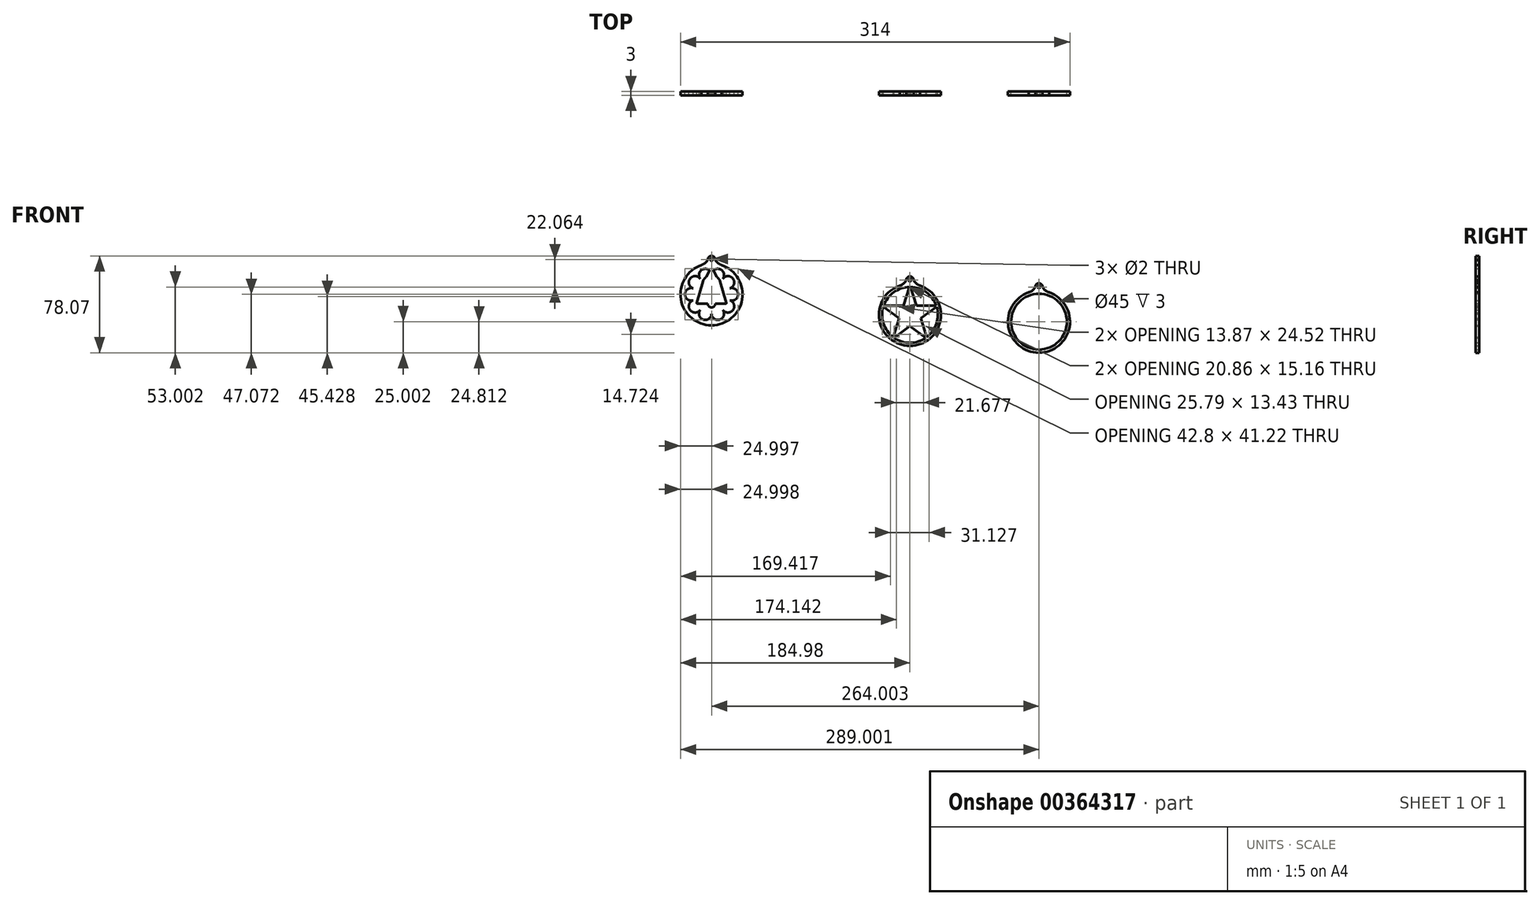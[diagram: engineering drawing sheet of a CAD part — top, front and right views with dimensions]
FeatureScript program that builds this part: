
annotation { "Feature Type Name" : "Feature", "Feature Type Description" : "" }
export const myFeature = defineFeature(function(context is Context, id is Id, definition is map)
    precondition{}
    {
        {
            var Q0;
            Q0=qCreatedBy(makeId("Front.planeOp"),FACE);
            var sketch = newSketch(context, id + "F0", { "sketchPlane" : qUnion([Q0])});
            skArc(sketch, "E0", {"start": v(-7.91, 23.72) * mm, "mid": v(0.08, -25) * mm, "end": v(7.76, 23.77) * mm});
            skPoint(sketch, "E1", {"position": v(0, 28) * mm});
            skArc(sketch, "E2", {"start": v(3, 27.85) * mm, "mid": v(0.08, 31) * mm, "end": v(-3, 28) * mm});
            skArc(sketch, "E3", {"start": v(3, 27.85) * mm, "mid": v(5.2, 25.22) * mm, "end": v(8.22, 23.6) * mm});
            skArc(sketch, "E4", {"start": v(-8.22, 23.6) * mm, "mid": v(-5.18, 25.29) * mm, "end": v(-3, 28) * mm});
            skCircle(sketch, "E5", {"center": v(0, 28) * mm, "radius": 1 * mm});
            skArc(sketch, "E6", {"start": v(-0.4, 22.5) * mm, "mid": v(-13.23, 18.2) * mm, "end": v(-21.27, 7.34) * mm});
            skCircle(sketch, "E7.cCircle", {"center": v(0, 0) * mm, "radius": 23.75 * mm, "construction": true});
            skLineSegment(sketch, "E8", {"start": v(-21.27, 7.34) * mm, "end": v(-5.33, 7.34) * mm});
            skLineSegment(sketch, "E9", {"start": v(21.52, 6.56) * mm, "end": v(8.63, -2.8) * mm});
            skLineSegment(sketch, "E10", {"start": v(-13.55, -17.96) * mm, "end": v(-8.63, -2.8) * mm});
            skLineSegment(sketch, "E11", {"start": v(0.4, 22.5) * mm, "end": v(5.33, 7.34) * mm});
            skLineSegment(sketch, "E12", {"start": v(-21.52, 6.56) * mm, "end": v(-8.63, -2.8) * mm});
            skArc(sketch, "E13.trimOffspring", {"start": v(21.27, 7.34) * mm, "mid": v(13.23, 18.2) * mm, "end": v(0.4, 22.5) * mm});
            skLineSegment(sketch, "E14.trimOffspring", {"start": v(8.63, -2.8) * mm, "end": v(13.55, -17.96) * mm});
            skLineSegment(sketch, "E15.trimOffspring", {"start": v(5.33, 7.34) * mm, "end": v(21.27, 7.34) * mm});
            skLineSegment(sketch, "E16.trimOffspring", {"start": v(-5.33, 7.34) * mm, "end": v(-0.4, 22.5) * mm});
            skLineSegment(sketch, "E17.trimOffspring", {"start": v(0, -9.07) * mm, "end": v(12.9, -18.44) * mm});
            skLineSegment(sketch, "E18.trimOffspring", {"start": v(0, -9.07) * mm, "end": v(-12.9, -18.44) * mm});
            skArc(sketch, "E19.trimOffspring", {"start": v(-21.52, 6.56) * mm, "mid": v(-21.4, -6.95) * mm, "end": v(-13.55, -17.96) * mm});
            skArc(sketch, "E20.trimOffspring", {"start": v(13.55, -17.96) * mm, "mid": v(21.4, -6.95) * mm, "end": v(21.52, 6.56) * mm});
            skArc(sketch, "E21.trimOffspring", {"start": v(-12.9, -18.44) * mm, "mid": v(0, -22.5) * mm, "end": v(12.9, -18.44) * mm});
            skArc(sketch, "E22", {"start": v(96.11, 18.2) * mm, "mid": v(104.1, -30.5) * mm, "end": v(111.78, 18.26) * mm});
            skPoint(sketch, "E23", {"position": v(104.02, 22.5) * mm});
            skArc(sketch, "E24", {"start": v(107.02, 22.34) * mm, "mid": v(104.1, 25.5) * mm, "end": v(101.02, 22.5) * mm});
            skArc(sketch, "E25", {"start": v(107.02, 22.34) * mm, "mid": v(109.22, 19.71) * mm, "end": v(112.24, 18.1) * mm});
            skArc(sketch, "E26", {"start": v(95.8, 18.1) * mm, "mid": v(98.84, 19.78) * mm, "end": v(101.02, 22.5) * mm});
            skCircle(sketch, "E27", {"center": v(104.02, 22.5) * mm, "radius": 1 * mm});
            skCircle(sketch, "E28.cCircle", {"center": v(104.02, -5.5) * mm, "radius": 23.75 * mm, "construction": true});
            skCircle(sketch, "E29", {"center": v(104.02, -5.5) * mm, "radius": 22.5 * mm});
            skArc(sketch, "E30", {"start": v(-167.9, 40.27) * mm, "mid": v(-159.9, -8.44) * mm, "end": v(-152.22, 40.32) * mm});
            skPoint(sketch, "E31", {"position": v(-159.98, 44.56) * mm});
            skArc(sketch, "E32", {"start": v(-156.99, 44.4) * mm, "mid": v(-159.9, 47.56) * mm, "end": v(-162.98, 44.56) * mm});
            skArc(sketch, "E33", {"start": v(-156.99, 44.4) * mm, "mid": v(-154.78, 41.78) * mm, "end": v(-151.76, 40.16) * mm});
            skArc(sketch, "E34", {"start": v(-168.2, 40.16) * mm, "mid": v(-165.16, 41.85) * mm, "end": v(-162.98, 44.56) * mm});
            skCircle(sketch, "E35", {"center": v(-159.98, 44.56) * mm, "radius": 1 * mm});
            skCircle(sketch, "E36.cCircle", {"center": v(-159.98, 16.56) * mm, "radius": 23.75 * mm, "construction": true});
            skLineSegment(sketch, "E37.0", {"start": v(-153.44, 36.93) * mm, "end": v(-153.3, 36.89) * mm});
            skLineSegment(sketch, "E37.1", {"start": v(-142.71, 29.2) * mm, "end": v(-142.63, 29.08) * mm});
            skLineSegment(sketch, "E37.2", {"start": v(-138.58, 16.63) * mm, "end": v(-138.58, 16.49) * mm});
            skLineSegment(sketch, "E37.3", {"start": v(-142.63, 4.04) * mm, "end": v(-142.71, 3.92) * mm});
            skLineSegment(sketch, "E37.4", {"start": v(-153.3, -3.77) * mm, "end": v(-153.44, -3.82) * mm});
            skLineSegment(sketch, "E37.5", {"start": v(-166.53, -3.82) * mm, "end": v(-166.66, -3.77) * mm});
            skLineSegment(sketch, "E37.6", {"start": v(-177.25, 3.92) * mm, "end": v(-177.34, 4.04) * mm});
            skLineSegment(sketch, "E37.7", {"start": v(-181.38, 16.49) * mm, "end": v(-181.38, 16.63) * mm});
            skLineSegment(sketch, "E37.8", {"start": v(-177.34, 29.08) * mm, "end": v(-177.25, 29.2) * mm});
            skLineSegment(sketch, "E37.9", {"start": v(-166.66, 36.89) * mm, "end": v(-166.53, 36.93) * mm});
            skPoint(sketch, "E38.visualSharp", {"position": v(-173.2, 34.76) * mm});
            skArc(sketch, "E38.filletArc", {"start": v(-166.66, 36.89) * mm, "mid": v(-169.87, 33.68) * mm, "end": v(-169.16, 29.2) * mm});
            skPoint(sketch, "E39.visualSharp", {"position": v(-159.98, 39.06) * mm});
            skArc(sketch, "E39.filletArc", {"start": v(-162.02, 36.2) * mm, "mid": v(-164.18, 37.1) * mm, "end": v(-166.53, 36.93) * mm});
            skArc(sketch, "E40.filletArc", {"start": v(-153.44, 36.93) * mm, "mid": v(-155.78, 37.1) * mm, "end": v(-157.95, 36.2) * mm});
            skPoint(sketch, "E41.visualSharp", {"position": v(-146.76, 34.76) * mm});
            skArc(sketch, "E41.filletArc", {"start": v(-150.8, 29.2) * mm, "mid": v(-150.1, 33.68) * mm, "end": v(-153.3, 36.89) * mm});
            skArc(sketch, "E42.filletArc", {"start": v(-142.71, 29.2) * mm, "mid": v(-146.76, 31.25) * mm, "end": v(-150.8, 29.2) * mm});
            skPoint(sketch, "E43.visualSharp", {"position": v(-138.58, 23.5) * mm});
            skArc(sketch, "E43.filletArc", {"start": v(-145.13, 21.38) * mm, "mid": v(-141.92, 24.6) * mm, "end": v(-142.63, 29.08) * mm});
            skPoint(sketch, "E44.visualSharp", {"position": v(-138.58, 9.6) * mm});
            skArc(sketch, "E44.filletArc", {"start": v(-145.13, 11.73) * mm, "mid": v(-140.64, 12.44) * mm, "end": v(-138.58, 16.49) * mm});
            skArc(sketch, "E45.filletArc", {"start": v(-138.58, 16.63) * mm, "mid": v(-140.64, 20.67) * mm, "end": v(-145.13, 21.38) * mm});
            skPoint(sketch, "E46.visualSharp", {"position": v(-146.76, -1.65) * mm});
            skArc(sketch, "E46.filletArc", {"start": v(-150.8, 3.92) * mm, "mid": v(-146.76, 1.86) * mm, "end": v(-142.71, 3.92) * mm});
            skArc(sketch, "E47.filletArc", {"start": v(-142.63, 4.04) * mm, "mid": v(-141.92, 8.52) * mm, "end": v(-145.13, 11.73) * mm});
            skArc(sketch, "E48.filletArc", {"start": v(-153.3, -3.77) * mm, "mid": v(-150.1, -0.56) * mm, "end": v(-150.8, 3.92) * mm});
            skPoint(sketch, "E49.visualSharp", {"position": v(-159.98, -5.94) * mm});
            skArc(sketch, "E49.filletArc", {"start": v(-159.98, 0.94) * mm, "mid": v(-157.92, -3.1) * mm, "end": v(-153.44, -3.82) * mm});
            skArc(sketch, "E50.filletArc", {"start": v(-166.53, -3.82) * mm, "mid": v(-162.04, -3.1) * mm, "end": v(-159.98, 0.94) * mm});
            skPoint(sketch, "E51.visualSharp", {"position": v(-173.2, -1.65) * mm});
            skArc(sketch, "E51.filletArc", {"start": v(-169.16, 3.92) * mm, "mid": v(-169.87, -0.56) * mm, "end": v(-166.66, -3.77) * mm});
            skPoint(sketch, "E52.visualSharp", {"position": v(-181.38, 9.6) * mm});
            skArc(sketch, "E52.filletArc", {"start": v(-174.84, 11.73) * mm, "mid": v(-178.05, 8.52) * mm, "end": v(-177.34, 4.04) * mm});
            skArc(sketch, "E53.filletArc", {"start": v(-177.25, 3.92) * mm, "mid": v(-173.2, 1.86) * mm, "end": v(-169.16, 3.92) * mm});
            skPoint(sketch, "E54.visualSharp", {"position": v(-181.38, 23.5) * mm});
            skArc(sketch, "E54.filletArc", {"start": v(-174.84, 21.38) * mm, "mid": v(-179.32, 20.67) * mm, "end": v(-181.38, 16.63) * mm});
            skArc(sketch, "E55.filletArc", {"start": v(-181.38, 16.49) * mm, "mid": v(-179.32, 12.44) * mm, "end": v(-174.84, 11.73) * mm});
            skArc(sketch, "E56.filletArc", {"start": v(-177.34, 29.08) * mm, "mid": v(-178.05, 24.6) * mm, "end": v(-174.84, 21.38) * mm});
            skArc(sketch, "E57.filletArc", {"start": v(-169.16, 29.2) * mm, "mid": v(-173.2, 31.25) * mm, "end": v(-177.25, 29.2) * mm});
            skLineSegment(sketch, "E58", {"start": v(-161.86, 35.53) * mm, "end": v(-164.41, 30.74) * mm});
            skLineSegment(sketch, "E59", {"start": v(-155.55, 30.74) * mm, "end": v(-158.1, 35.53) * mm});
            skPoint(sketch, "E60.visualSharp", {"position": v(-165.19, 29.28) * mm});
            skArc(sketch, "E60.filletArc", {"start": v(-165.48, 29.37) * mm, "mid": v(-164.89, 30) * mm, "end": v(-164.41, 30.74) * mm});
            skPoint(sketch, "E61.visualSharp", {"position": v(-154.78, 29.28) * mm});
            skArc(sketch, "E61.filletArc", {"start": v(-155.55, 30.74) * mm, "mid": v(-155.08, 30) * mm, "end": v(-154.48, 29.37) * mm});
            skLineSegment(sketch, "E62", {"start": v(-166.94, 27.05) * mm, "end": v(-171.97, 9.69) * mm});
            skLineSegment(sketch, "E63", {"start": v(-171.47, 9) * mm, "end": v(-163.02, 9) * mm});
            skLineSegment(sketch, "E64", {"start": v(-148, 9.69) * mm, "end": v(-153.02, 27.05) * mm});
            skPoint(sketch, "E65.visualSharp", {"position": v(-166.47, 28.68) * mm});
            skArc(sketch, "E65.filletArc", {"start": v(-165.48, 29.37) * mm, "mid": v(-166.38, 28.31) * mm, "end": v(-166.94, 27.05) * mm});
            skPoint(sketch, "E66.visualSharp", {"position": v(-153.5, 28.68) * mm});
            skArc(sketch, "E66.filletArc", {"start": v(-153.02, 27.05) * mm, "mid": v(-153.59, 28.31) * mm, "end": v(-154.48, 29.37) * mm});
            skPoint(sketch, "E67.visualSharp", {"position": v(-161.66, 35.9) * mm});
            skArc(sketch, "E67.filletArc", {"start": v(-161.86, 35.53) * mm, "mid": v(-161.81, 35.9) * mm, "end": v(-162.02, 36.2) * mm});
            skPoint(sketch, "E68.visualSharp", {"position": v(-158.3, 35.9) * mm});
            skArc(sketch, "E68.filletArc", {"start": v(-157.95, 36.2) * mm, "mid": v(-158.15, 35.9) * mm, "end": v(-158.1, 35.53) * mm});
            skPoint(sketch, "E69.visualSharp", {"position": v(-172.17, 9) * mm});
            skArc(sketch, "E69.filletArc", {"start": v(-171.97, 9.69) * mm, "mid": v(-171.89, 9.22) * mm, "end": v(-171.47, 9) * mm});
            skPoint(sketch, "E70.visualSharp", {"position": v(-147.8, 9) * mm});
            skArc(sketch, "E70.filletArc", {"start": v(-148.5, 9) * mm, "mid": v(-148.08, 9.22) * mm, "end": v(-148, 9.69) * mm});
            skArc(sketch, "E71", {"start": v(-163.02, 9) * mm, "mid": v(-159.98, 5.97) * mm, "end": v(-156.94, 9) * mm});
            skLineSegment(sketch, "E72.trimOffspring", {"start": v(-156.94, 9) * mm, "end": v(-148.5, 9) * mm});
            skSolve(sketch);
        }
        {
            var Q0;
            {var subQ4=sQuery(id+"F0.wireOp",EDGE,"E24");Q0=makeQuery(id+"F0.imprint","IMPRINT",FACE,{"disambiguationData":[TD([[makeQuery(id+"F0.imprint","IMPRINT",EDGE,{"derivedFrom":subQ4}),1.0]])]});}
            var Q1;
            {var subQ3=sQuery(id+"F0.wireOp",EDGE,"E2");Q1=makeQuery(id+"F0.imprint","IMPRINT",FACE,{"disambiguationData":[TD([[makeQuery(id+"F0.imprint","IMPRINT",EDGE,{"derivedFrom":subQ3}),1.0]])]});}
            var Q2;
            {var subQ3=sQuery(id+"F0.wireOp",EDGE,"E32");Q2=makeQuery(id+"F0.imprint","IMPRINT",FACE,{"disambiguationData":[TD([[makeQuery(id+"F0.imprint","IMPRINT",EDGE,{"derivedFrom":subQ3}),1.0]])]});}
            extrude(context, id + "F1", {"entities" : qUnion([Q0, Q1, Q2]), "depth" : 3 * mm});
        }
    });
